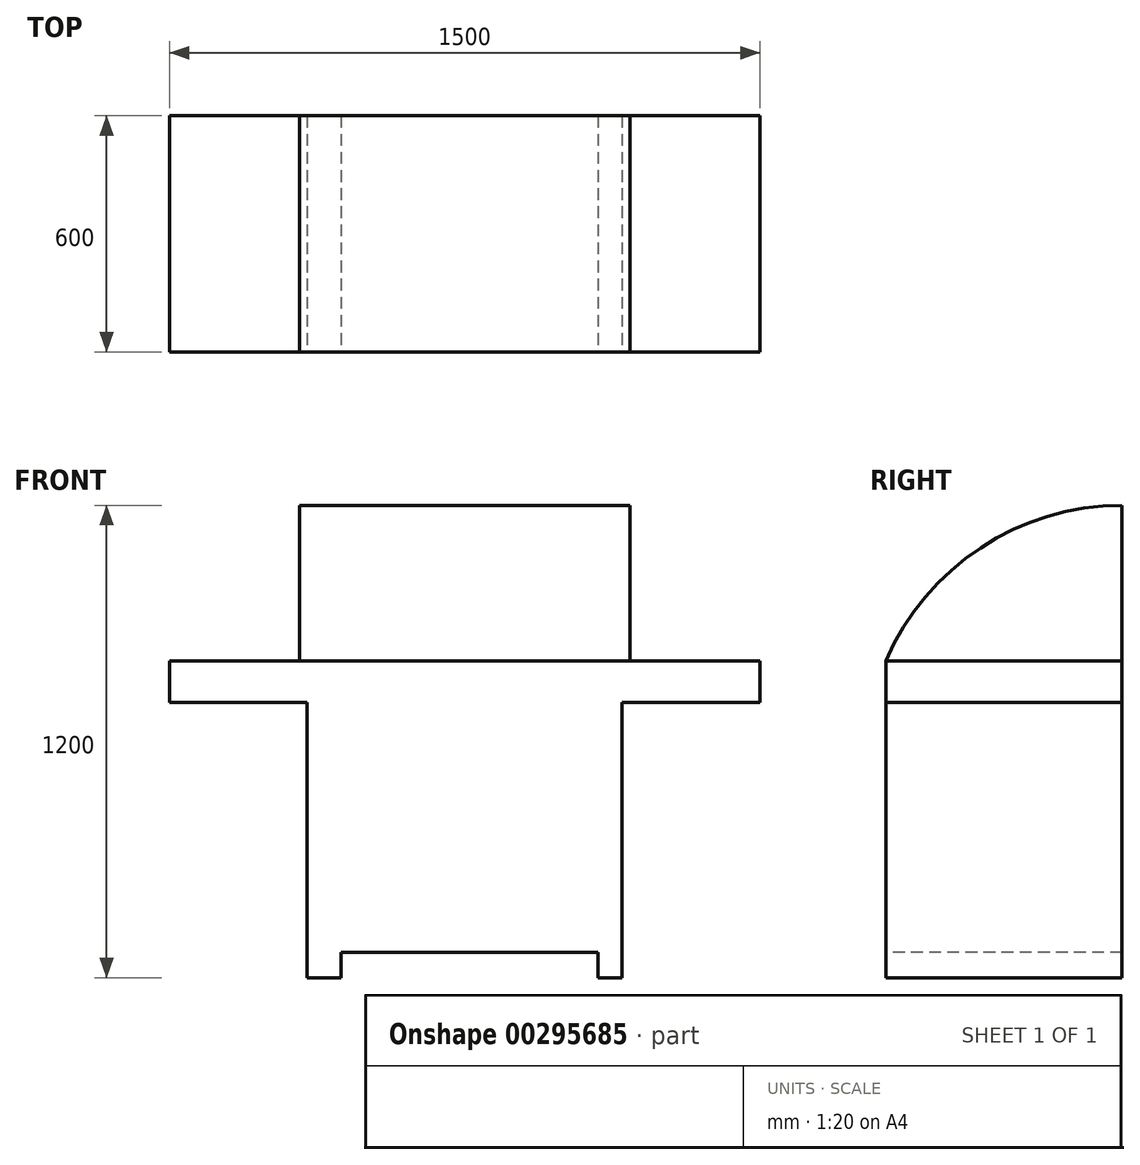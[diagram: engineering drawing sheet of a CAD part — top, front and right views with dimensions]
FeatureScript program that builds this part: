
annotation { "Feature Type Name" : "Feature", "Feature Type Description" : "" }
export const myFeature = defineFeature(function(context is Context, id is Id, definition is map)
    precondition{}
    {
        {
            var Q0;
            Q0=qCreatedBy(makeId("Top.planeOp"),FACE);
            var sketch = newSketch(context, id + "F0", { "sketchPlane" : qUnion([Q0])});
            skLineSegment(sketch, "E0.bottom", {"start": v(-750, -300) * mm, "end": v(750, -300) * mm});
            skLineSegment(sketch, "E0.top", {"start": v(-750, 300) * mm, "end": v(750, 300) * mm});
            skLineSegment(sketch, "E0.left", {"start": v(-750, -300) * mm, "end": v(-750, 300) * mm});
            skLineSegment(sketch, "E0.right", {"start": v(750, -300) * mm, "end": v(750, 300) * mm});
            skPoint(sketch, "E0.middle", {"position": v(0, 0) * mm});
            skSolve(sketch);
        }
        {
            var Q0;
            Q0 = qSketchRegion(id + "F0", true);
            extrude(context, id + "F1", {"entities" : qUnion([Q0]), "depth" : 1200 * mm});
        }
        {
            var Q0;
            Q0=makeQuery(id+"F1.opExtrude","SWEPT_FACE",FACE,{"disambiguationData":[OSD([sQuery(id+"F0.wireOp",EDGE,"E0.right")])]});
            var sketch = newSketch(context, id + "F2", { "sketchPlane" : qUnion([Q0])});
            skArc(sketch, "E1", {"start": v(300, 1200) * mm, "mid": v(-59.2, 1092.35) * mm, "end": v(-300, 804.89) * mm});
            skLineSegment(sketch, "E2", {"start": v(-300, 804.89) * mm, "end": v(-300, 1200) * mm});
            skLineSegment(sketch, "E3", {"start": v(-300, 1200) * mm, "end": v(300, 1200) * mm});
            skSolve(sketch);
        }
        {
            var Q0;
            Q0 = qSketchRegion(id + "F2", true);
            extrude(context, id + "F3", {"entities" : qUnion([Q0]), "operationType" : NewBodyOperationType.REMOVE, "oppositeDirection" : true, "depth" : 1600 * mm});
        }
        {
            var Q0;
            Q0=makeQuery(id+"F1.opExtrude","SWEPT_FACE",FACE,{"disambiguationData":[OSD([sQuery(id+"F0.wireOp",EDGE,"E0.bottom")])]});
            var sketch = newSketch(context, id + "F4", { "sketchPlane" : qUnion([Q0])});
            skLineSegment(sketch, "E4.bottom", {"start": v(-750, 0) * mm, "end": v(-400, 0) * mm});
            skLineSegment(sketch, "E4.top", {"start": v(-750, 700) * mm, "end": v(-400, 700) * mm});
            skLineSegment(sketch, "E4.left", {"start": v(-750, 0) * mm, "end": v(-750, 700) * mm});
            skLineSegment(sketch, "E4.right", {"start": v(-400, 0) * mm, "end": v(-400, 700) * mm});
            skLineSegment(sketch, "E5.bottom", {"start": v(750, 0) * mm, "end": v(400, 0) * mm});
            skLineSegment(sketch, "E5.top", {"start": v(750, 700) * mm, "end": v(400, 700) * mm});
            skLineSegment(sketch, "E5.left", {"start": v(750, 0) * mm, "end": v(750, 700) * mm});
            skLineSegment(sketch, "E5.right", {"start": v(400, 0) * mm, "end": v(400, 700) * mm});
            skSolve(sketch);
        }
        {
            var Q0;
            Q0 = qSketchRegion(id + "F4", true);
            extrude(context, id + "F5", {"entities" : qUnion([Q0]), "operationType" : NewBodyOperationType.REMOVE, "oppositeDirection" : true, "depth" : 1500 * mm});
        }
        {
            var Q0;
            Q0=makeQuery(id+"F1.opExtrude","SWEPT_FACE",FACE,{"disambiguationData":[OSD([sQuery(id+"F0.wireOp",EDGE,"E0.bottom")])]});
            var sketch = newSketch(context, id + "F6", { "sketchPlane" : qUnion([Q0])});
            skLineSegment(sketch, "E6.bottom", {"start": v(-750, 804.89) * mm, "end": v(-420, 804.89) * mm});
            skLineSegment(sketch, "E6.top", {"start": v(-750, 1224.89) * mm, "end": v(-420, 1224.89) * mm});
            skLineSegment(sketch, "E6.left", {"start": v(-750, 804.89) * mm, "end": v(-750, 1224.89) * mm});
            skLineSegment(sketch, "E6.right", {"start": v(-420, 804.89) * mm, "end": v(-420, 1224.89) * mm});
            skLineSegment(sketch, "E7.bottom", {"start": v(750, 804.89) * mm, "end": v(420, 804.89) * mm});
            skLineSegment(sketch, "E7.top", {"start": v(750, 1224.89) * mm, "end": v(420, 1224.89) * mm});
            skLineSegment(sketch, "E7.left", {"start": v(750, 804.89) * mm, "end": v(750, 1224.89) * mm});
            skLineSegment(sketch, "E7.right", {"start": v(420, 804.89) * mm, "end": v(420, 1224.89) * mm});
            skSolve(sketch);
        }
        {
            var Q0;
            Q0 = qSketchRegion(id + "F6", true);
            extrude(context, id + "F7", {"entities" : qUnion([Q0]), "operationType" : NewBodyOperationType.REMOVE, "oppositeDirection" : true, "depth" : 2000 * mm});
        }
        {
            var Q0;
            Q0=makeQuery(id+"F1.opExtrude","SWEPT_FACE",FACE,{"disambiguationData":[OSD([sQuery(id+"F0.wireOp",EDGE,"E0.bottom")])]});
            var sketch = newSketch(context, id + "F8", { "sketchPlane" : qUnion([Q0])});
            skLineSegment(sketch, "E8.bottom", {"start": v(-314.62, 0) * mm, "end": v(338.7, 0) * mm});
            skLineSegment(sketch, "E8.top", {"start": v(-314.62, 64.88) * mm, "end": v(338.7, 64.88) * mm});
            skLineSegment(sketch, "E8.left", {"start": v(-314.62, 0) * mm, "end": v(-314.62, 64.88) * mm});
            skLineSegment(sketch, "E8.right", {"start": v(338.7, 0) * mm, "end": v(338.7, 64.88) * mm});
            skSolve(sketch);
        }
        {
            var Q0;
            Q0 = qSketchRegion(id + "F8", true);
            extrude(context, id + "F9", {"entities" : qUnion([Q0]), "operationType" : NewBodyOperationType.REMOVE, "oppositeDirection" : true, "depth" : 1500 * mm});
        }
    });
